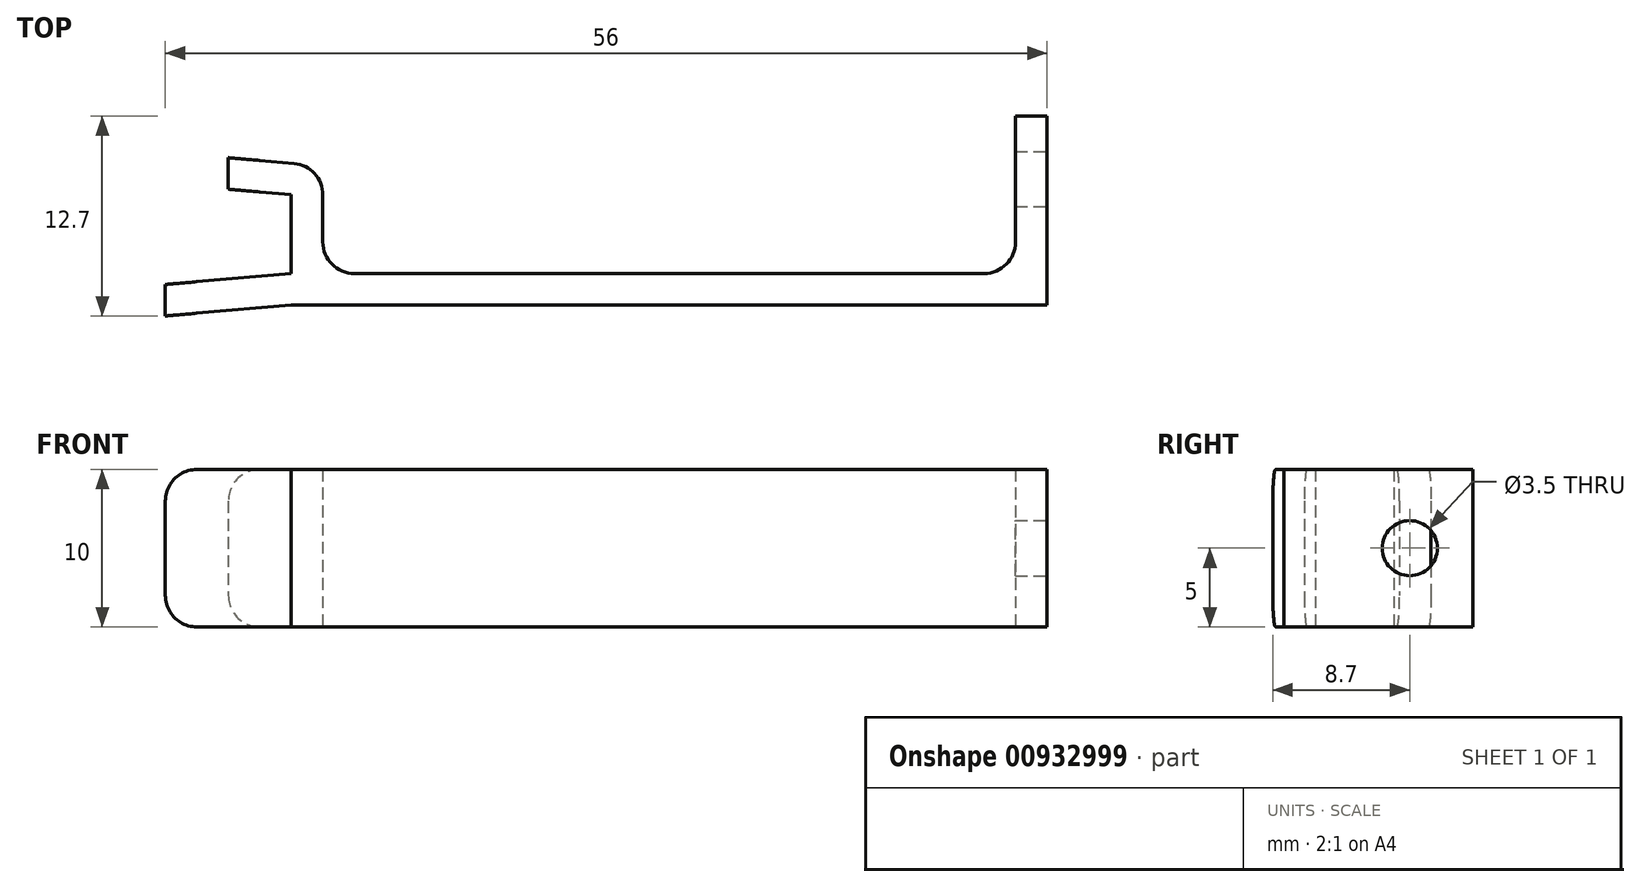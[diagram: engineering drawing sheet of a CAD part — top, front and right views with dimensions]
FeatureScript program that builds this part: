
annotation { "Feature Type Name" : "Feature", "Feature Type Description" : "" }
export const myFeature = defineFeature(function(context is Context, id is Id, definition is map)
    precondition{}
    {
        {
            var Q0;
            Q0=qCreatedBy(makeId("Top.planeOp"),FACE);
            var sketch = newSketch(context, id + "F0", { "sketchPlane" : qUnion([Q0])});
            skLineSegment(sketch, "E0", {"start": v(48, 0) * mm, "end": v(48, 12) * mm});
            skLineSegment(sketch, "E1", {"start": v(48, 12) * mm, "end": v(46, 12) * mm});
            skLineSegment(sketch, "E2", {"start": v(46, 12) * mm, "end": v(46, 2) * mm});
            skLineSegment(sketch, "E3", {"start": v(46, 2) * mm, "end": v(2, 2) * mm});
            skLineSegment(sketch, "E4", {"start": v(2, 2) * mm, "end": v(2, 8.83) * mm});
            skLineSegment(sketch, "E5", {"start": v(2, 8.83) * mm, "end": v(-4, 9.35) * mm});
            skLineSegment(sketch, "E6", {"start": v(-4, 9.35) * mm, "end": v(-4, 7.35) * mm});
            skLineSegment(sketch, "E7", {"start": v(-4, 7.35) * mm, "end": v(0, 7) * mm});
            skLineSegment(sketch, "E8", {"start": v(0, 7) * mm, "end": v(0, 2) * mm});
            skLineSegment(sketch, "E9", {"start": v(0, 2) * mm, "end": v(-8, 1.3) * mm});
            skLineSegment(sketch, "E10", {"start": v(-8, 1.3) * mm, "end": v(-8, -0.7) * mm});
            skLineSegment(sketch, "E11", {"start": v(-8, -0.7) * mm, "end": v(0, 0) * mm});
            skLineSegment(sketch, "E12", {"start": v(0, 0) * mm, "end": v(48, 0) * mm});
            skSolve(sketch);
        }
        {
            var Q0;
            Q0=makeQuery(id+"F0.imprint","IMPRINT",FACE,{"disambiguationData":[TD([[makeQuery(id+"F0.imprint","IMPRINT",EDGE,{"derivedFrom":sQuery(id+"F0.wireOp",EDGE,"E0")}),1.0]])]});
            extrude(context, id + "F1", {"entities" : qUnion([Q0]), "depth" : 10 * mm, "offsetDistance" : 25 * mm});
        }
        {
            var Q0;
            Q0=makeQuery(id+"F1.opExtrude","CAP_EDGE",EDGE,{"disambiguationData":[OSD([sQuery(id+"F0.wireOp",EDGE,"E10")])],"isStart":false});
            var Q1;
            Q1=makeQuery(id+"F1.opExtrude","CAP_EDGE",EDGE,{"disambiguationData":[OSD([sQuery(id+"F0.wireOp",EDGE,"E10")])],"isStart":true});
            var Q2;
            Q2=makeQuery(id+"F1.opExtrude","CAP_EDGE",EDGE,{"disambiguationData":[OSD([sQuery(id+"F0.wireOp",EDGE,"E6")])],"isStart":true});
            var Q3;
            Q3=makeQuery(id+"F1.opExtrude","CAP_EDGE",EDGE,{"disambiguationData":[OSD([sQuery(id+"F0.wireOp",EDGE,"E6")])],"isStart":false});
            var Q4;
            Q4=makeQuery(id+"F1.opExtrude","SWEPT_EDGE",EDGE,{"disambiguationData":[OSD([sQuery(id+"F0.wireOp",EDGE,"E3"),sQuery(id+"F0.wireOp",EDGE,"E4")])]});
            var Q5;
            Q5=makeQuery(id+"F1.opExtrude","SWEPT_EDGE",EDGE,{"disambiguationData":[OSD([sQuery(id+"F0.wireOp",EDGE,"E4"),sQuery(id+"F0.wireOp",EDGE,"E5")])]});
            var Q6;
            Q6=makeQuery(id+"F1.opExtrude","SWEPT_EDGE",EDGE,{"disambiguationData":[OSD([sQuery(id+"F0.wireOp",EDGE,"E2"),sQuery(id+"F0.wireOp",EDGE,"E3")])]});
            fillet(context, id + "F2", {"entities" : qUnion([Q0, Q1, Q2, Q3, Q4, Q5, Q6]), "radius" : 2 * mm, "tangentPropagation" : true, "allowEdgeOverflow" : false});
        }
        {
            var Q0;
            Q0=makeQuery(id+"F1.opExtrude","SWEPT_FACE",FACE,{"disambiguationData":[OSD([sQuery(id+"F0.wireOp",EDGE,"E2")])]});
            var sketch = newSketch(context, id + "F3", { "sketchPlane" : qUnion([Q0])});
            skPoint(sketch, "E13", {"position": v(-8, 5) * mm});
            skSolve(sketch);
        }
        {
            var Q0;
            Q0=sQuery(id+"F3.wireOp",VERTEX,"E13");
            var Q1;
            Q1=makeQuery(id+"F1.opExtrude","SWEPT_BODY",BODY,{"disambiguationData":[OSD([sQuery(id+"F0.wireOp",EDGE,"E0"),sQuery(id+"F0.wireOp",EDGE,"E1"),sQuery(id+"F0.wireOp",EDGE,"E2"),sQuery(id+"F0.wireOp",EDGE,"E3"),sQuery(id+"F0.wireOp",EDGE,"E4"),sQuery(id+"F0.wireOp",EDGE,"E5"),sQuery(id+"F0.wireOp",EDGE,"E6"),sQuery(id+"F0.wireOp",EDGE,"E7"),sQuery(id+"F0.wireOp",EDGE,"E8"),sQuery(id+"F0.wireOp",EDGE,"E9"),sQuery(id+"F0.wireOp",EDGE,"E10"),sQuery(id+"F0.wireOp",EDGE,"E11"),sQuery(id+"F0.wireOp",EDGE,"E12")])]});
            hole(context, id + "F4", {"style" : HoleStyle.SIMPLE, "endStyle" : HoleEndStyle.THROUGH, "holeDiameter" : 3.5 * mm, "majorDiameter" : 5 * mm, "isTappedThrough" : true, "tappedDepth" : 12 * mm, "tapClearance" : 3, "locations" : qUnion([Q0]), "scope" : qUnion([Q1]), "startStyle" : HoleStartStyle.PART});
        }
    });
